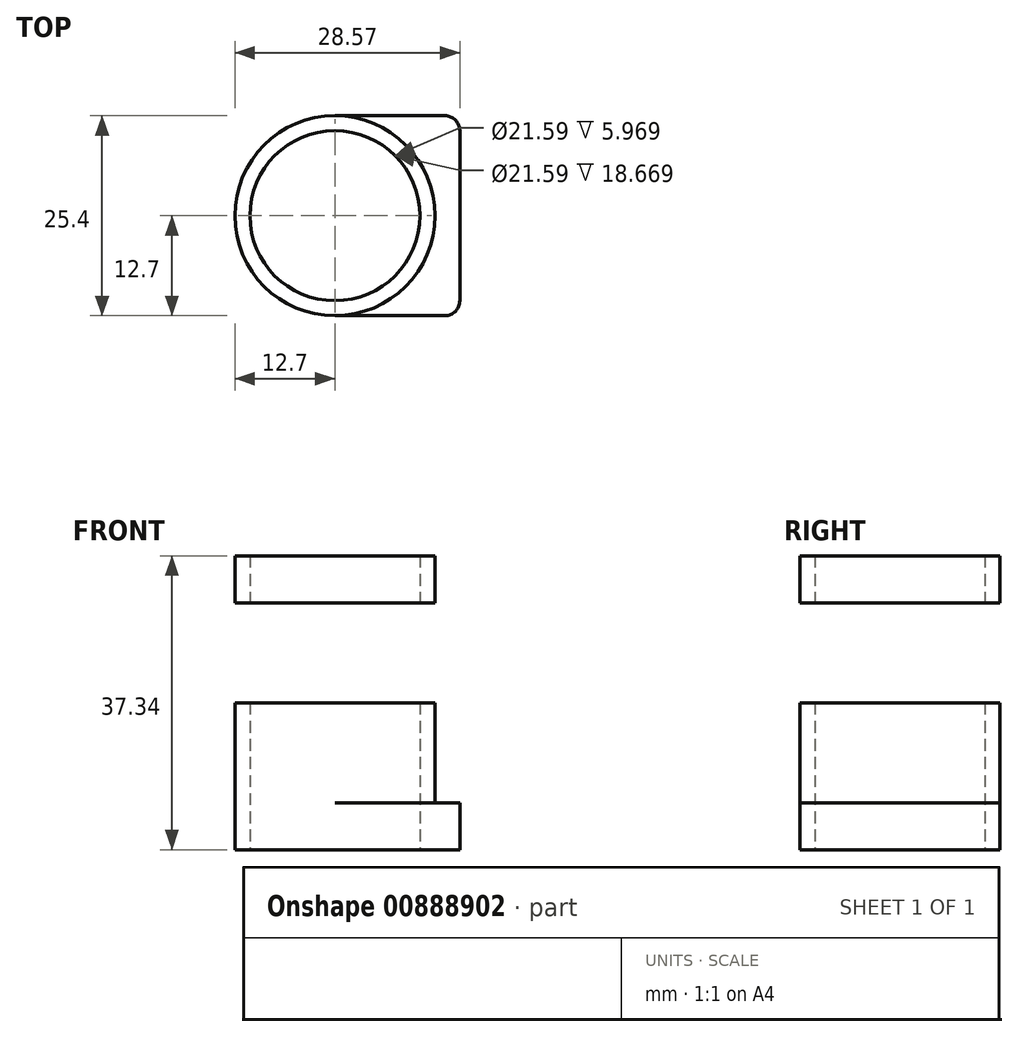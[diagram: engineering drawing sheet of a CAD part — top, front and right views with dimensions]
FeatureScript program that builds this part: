
annotation { "Feature Type Name" : "Feature", "Feature Type Description" : "" }
export const myFeature = defineFeature(function(context is Context, id is Id, definition is map)
    precondition{}
    {
        {
            var Q0;
            Q0=qCreatedBy(makeId("Top.planeOp"),FACE);
            var sketch = newSketch(context, id + "F0", { "sketchPlane" : qUnion([Q0])});
            skCircle(sketch, "E0", {"center": v(0, 0) * mm, "radius": 12.7 * mm});
            skCircle(sketch, "E1", {"center": v(0, 0) * mm, "radius": 10.8 * mm});
            skSolve(sketch);
        }
        {
            var Q0;
            Q0=qCreatedBy(makeId("Top.planeOp"),FACE);
            var sketch = newSketch(context, id + "F1", { "sketchPlane" : qUnion([Q0])});
            skLineSegment(sketch, "E2", {"start": v(0, -12.7) * mm, "end": v(13.97, -12.7) * mm});
            skLineSegment(sketch, "E3", {"start": v(15.87, -10.8) * mm, "end": v(15.87, 10.8) * mm});
            skLineSegment(sketch, "E4", {"start": v(13.97, 12.7) * mm, "end": v(0, 12.7) * mm});
            skCircle(sketch, "E5", {"center": v(13.97, -10.8) * mm, "radius": 1.9 * mm});
            skCircle(sketch, "E6.MirrorC", {"center": v(13.97, 10.8) * mm, "radius": 1.9 * mm});
            skPoint(sketch, "E7.MirrorCS.end.orphan", {"position": v(13.97, 8.9) * mm});
            skPoint(sketch, "E7.MirrorCS.start.orphan", {"position": v(15.87, 8.9) * mm});
            skPoint(sketch, "E8.end.orphan", {"position": v(13.97, -8.9) * mm});
            skPoint(sketch, "E8.start.orphan", {"position": v(15.87, -8.9) * mm});
            skArc(sketch, "E9", {"start": v(0, -12.7) * mm, "mid": v(12.7, 0) * mm, "end": v(0, 12.7) * mm});
            skSolve(sketch);
        }
        {
            var Q0;
            Q0=makeQuery(id+"F0.imprint","IMPRINT",FACE,{"disambiguationData":[TD([[makeQuery(id+"F0.imprint","IMPRINT",EDGE,{"derivedFrom":sQuery(id+"F0.wireOp",EDGE,"E0")}),1.0]])]});
            var Q1;
            {var subQ0=sQuery(id+"F1.wireOp",EDGE,"E6.MirrorC");var subQ1=makeQuery(id+"F1.imprint","INTERSECT",VERTEX,{"derivedFrom":[sQuery(id+"F1.wireOp",EDGE,"E3"),subQ0]});Q1=makeQuery(id+"F1.imprint","IMPRINT",FACE,{"disambiguationData":[TD([[makeQuery(id+"F1.imprint","IMPRINT",EDGE,{"disambiguationData":[TD([[subQ1,-1.0]])],"derivedFrom":subQ0}),-1.0]])]});}
            var Q2;
            {var subQ0=sQuery(id+"F1.wireOp",EDGE,"E5");var subQ1=makeQuery(id+"F1.imprint","INTERSECT",VERTEX,{"derivedFrom":[sQuery(id+"F1.wireOp",EDGE,"E2"),subQ0]});Q2=makeQuery(id+"F1.imprint","IMPRINT",FACE,{"disambiguationData":[TD([[makeQuery(id+"F1.imprint","IMPRINT",EDGE,{"disambiguationData":[TD([[subQ1,-1.0]])],"derivedFrom":subQ0}),-1.0]])]});}
            extrude(context, id + "F2", {"entities" : qUnion([Q0, Q1, Q2]), "flatOperationType" : FlatOperationType.REMOVE, "depth" : 12.7 * mm, "offsetDistance" : 25.4 * mm, "domain" : OperationDomain.MODEL});
        }
        {
            var Q0;
            Q0 = qSketchRegion(id + "F0", true);
            var Q1;
            Q1 = qSketchRegion(id + "F1", true);
            var Q2;
            Q2=makeQuery(id+"F2.opExtrude","CAP_FACE",FACE,{"disambiguationData":[OSD([sQuery(id+"F1.wireOp",EDGE,"E6.MirrorC")])],"isStart":true});
            var Q3;
            Q3=makeQuery(id+"F2.opExtrude","CAP_FACE",FACE,{"disambiguationData":[OSD([sQuery(id+"F0.wireOp",EDGE,"E0"),sQuery(id+"F0.wireOp",EDGE,"E1")])],"isStart":true});
            var Q4;
            Q4=makeQuery(id+"F2.opExtrude","CAP_FACE",FACE,{"disambiguationData":[OSD([sQuery(id+"F1.wireOp",EDGE,"E5")])],"isStart":true});
            extrude(context, id + "F3", {"entities" : qUnion([Q0, Q1, Q2, Q3, Q4]), "oppositeDirection" : true, "depth" : 5.97 * mm, "offsetDistance" : 25.4 * mm});
        }
        {
            var Q0;
            Q0=makeQuery(id+"F2.opExtrude","CAP_FACE",FACE,{"disambiguationData":[OSD([sQuery(id+"F0.wireOp",EDGE,"E0"),sQuery(id+"F0.wireOp",EDGE,"E1")])],"isStart":false});
            cPlane(context, id + "F4", {"entities" : qUnion([Q0]), "cplaneType" : CPlaneType.OFFSET, "offset" : 0 * mm, "width" : 152.4 * mm, "height" : 152.4 * mm});
        }
        {
            var Q0;
            {var subQ0=sQuery(id+"F0.wireOp",EDGE,"E1");var subQ1=sQuery(id+"F0.wireOp",EDGE,"E0");Q0=makeQuery(id+"F3.opExtrude","SWEPT_BODY",BODY,{"disambiguationData":[OSD([subQ1,subQ0]),TDD([makeQuery(id+"F2.opExtrude","CAP_FACE",FACE,{"disambiguationData":[OSD([subQ1,subQ0])],"isStart":true})])]});}
            var Q1;
            Q1=qCreatedBy(id+"F4.planeOp",FACE);
            mirror(context, id + "F5", {"operationType" : NewBodyOperationType.ADD, "entities" : qUnion([Q0]), "mirrorPlane" : qUnion([Q1])});
        }
    });
